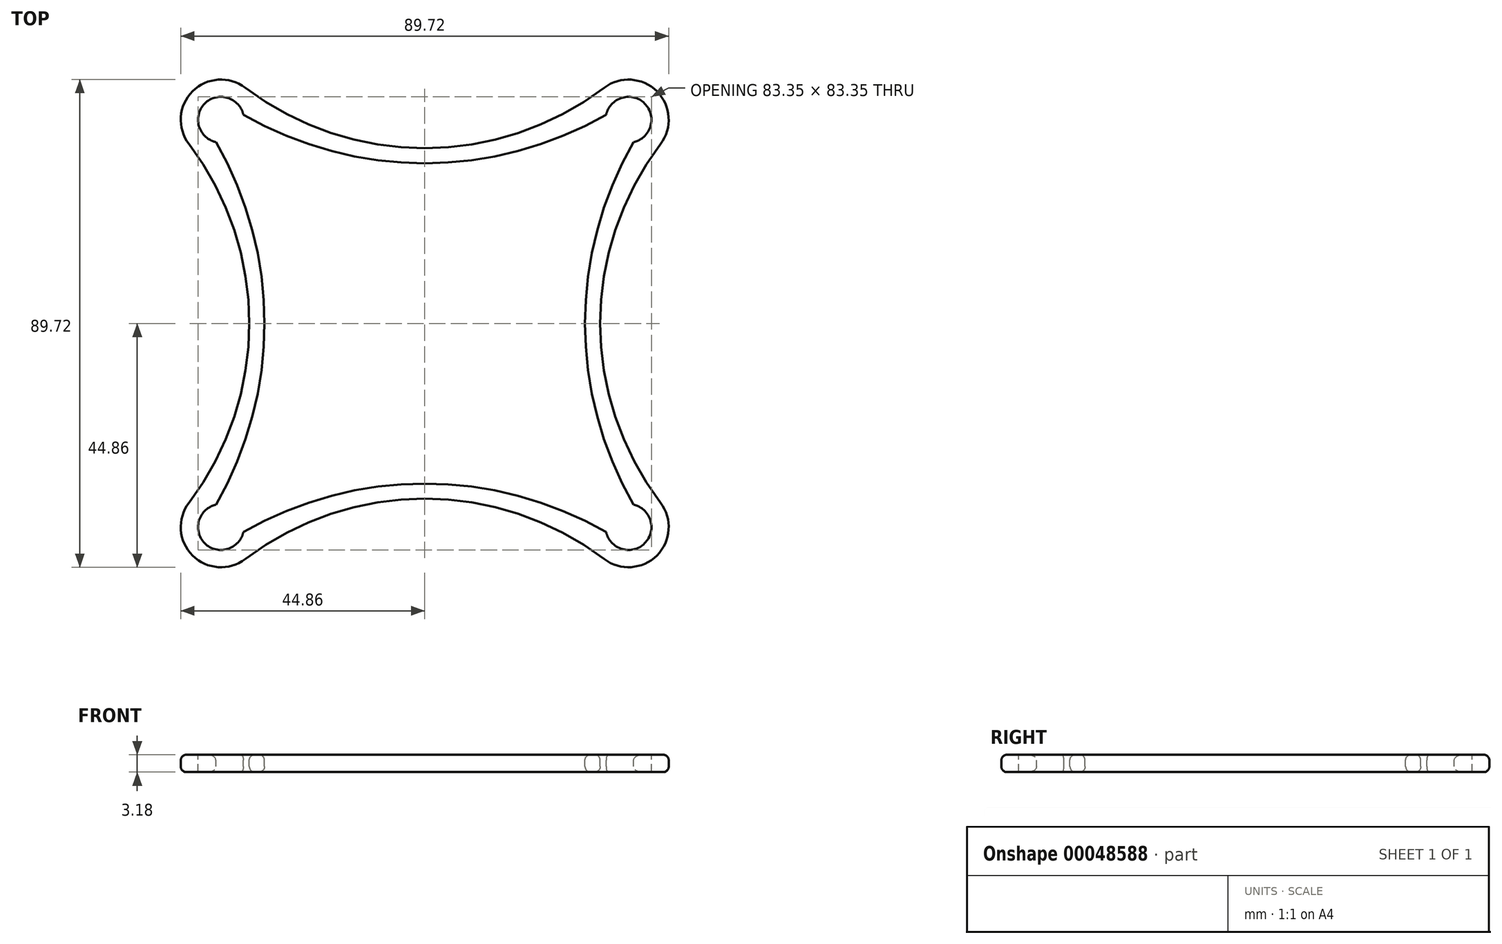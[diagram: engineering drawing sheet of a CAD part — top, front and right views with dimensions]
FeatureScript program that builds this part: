
annotation { "Feature Type Name" : "Feature", "Feature Type Description" : "" }
export const myFeature = defineFeature(function(context is Context, id is Id, definition is map)
    precondition{}
    {
        {
            var Q0;
            Q0=qCreatedBy(makeId("Top.planeOp"),FACE);
            var sketch = newSketch(context, id + "F0", { "sketchPlane" : qUnion([Q0])});
            skCircle(sketch, "E0", {"center": v(-37.47, 37.47) * mm, "radius": 4.22 * mm});
            skCircle(sketch, "E1", {"center": v(37.47, 37.47) * mm, "radius": 4.22 * mm});
            skCircle(sketch, "E2", {"center": v(37.47, -37.47) * mm, "radius": 4.22 * mm});
            skCircle(sketch, "E3", {"center": v(-37.47, -37.47) * mm, "radius": 4.22 * mm});
            skCircle(sketch, "E4", {"center": v(-37.47, 37.47) * mm, "radius": 7.4 * mm});
            skCircle(sketch, "E5", {"center": v(-37.47, -37.47) * mm, "radius": 7.4 * mm});
            skCircle(sketch, "E6", {"center": v(37.47, -37.47) * mm, "radius": 7.4 * mm});
            skCircle(sketch, "E7", {"center": v(37.47, 37.47) * mm, "radius": 7.4 * mm});
            skCircle(sketch, "E8", {"center": v(-96.14, 0) * mm, "radius": 66.68 * mm});
            skCircle(sketch, "E9", {"center": v(-86.87, 0) * mm, "radius": 54.61 * mm});
            skCircle(sketch, "E10", {"center": v(0, 96.14) * mm, "radius": 66.68 * mm});
            skCircle(sketch, "E11", {"center": v(0, 86.87) * mm, "radius": 54.61 * mm});
            skCircle(sketch, "E12", {"center": v(96.14, 0) * mm, "radius": 66.68 * mm});
            skCircle(sketch, "E13", {"center": v(86.87, 0) * mm, "radius": 54.61 * mm});
            skCircle(sketch, "E14", {"center": v(0, -96.14) * mm, "radius": 66.68 * mm});
            skCircle(sketch, "E15", {"center": v(0, -86.87) * mm, "radius": 54.61 * mm});
            skSolve(sketch);
        }
        {
            var Q0;
            {var subQ3=sQuery(id+"F0.wireOp",EDGE,"E4");var subQ5=sQuery(id+"F0.wireOp",EDGE,"E9");var subQ7=makeQuery(id+"F0.imprint","INTERSECT",VERTEX,{"derivedFrom":[subQ3,subQ5]});Q0=makeQuery(id+"F0.imprint","IMPRINT",FACE,{"disambiguationData":[TD([[makeQuery(id+"F0.imprint","IMPRINT",EDGE,{"disambiguationData":[TD([[subQ7,-1.0]])],"derivedFrom":subQ3}),-1.0]])]});}
            var Q1;
            {var subQ0=sQuery(id+"F0.wireOp",EDGE,"E8");var subQ1=sQuery(id+"F0.wireOp",EDGE,"E0");var subQ2=makeQuery(id+"F0.imprint","INTERSECT",VERTEX,{"disambiguationData":[OD(0.0)],"derivedFrom":[subQ1,subQ0]});Q1=makeQuery(id+"F0.imprint","IMPRINT",FACE,{"disambiguationData":[TD([[makeQuery(id+"F0.imprint","IMPRINT",EDGE,{"disambiguationData":[TD([[subQ2,-1.0]])],"derivedFrom":subQ1}),-1.0]])]});}
            var Q2;
            {var subQ0=sQuery(id+"F0.wireOp",EDGE,"E10");var subQ1=sQuery(id+"F0.wireOp",EDGE,"E0");var subQ2=makeQuery(id+"F0.imprint","INTERSECT",VERTEX,{"disambiguationData":[OD(0.0)],"derivedFrom":[subQ1,subQ0]});Q2=makeQuery(id+"F0.imprint","IMPRINT",FACE,{"disambiguationData":[TD([[makeQuery(id+"F0.imprint","IMPRINT",EDGE,{"disambiguationData":[TD([[subQ2,-1.0]])],"derivedFrom":subQ1}),-1.0]])]});}
            var Q3;
            {var subQ0=sQuery(id+"F0.wireOp",EDGE,"E0");var subQ1=sQuery(id+"F0.wireOp",EDGE,"E10");var subQ3=makeQuery(id+"F0.imprint","INTERSECT",VERTEX,{"disambiguationData":[OD(0.0)],"derivedFrom":[subQ0,subQ1]});Q3=makeQuery(id+"F0.imprint","IMPRINT",FACE,{"disambiguationData":[TD([[makeQuery(id+"F0.imprint","IMPRINT",EDGE,{"disambiguationData":[TD([[subQ3,1.0]])],"derivedFrom":subQ0}),-1.0]])]});}
            var Q4;
            {var subQ0=sQuery(id+"F0.wireOp",EDGE,"E11");var subQ3=sQuery(id+"F0.wireOp",EDGE,"E4");var subQ4=makeQuery(id+"F0.imprint","INTERSECT",VERTEX,{"derivedFrom":[subQ3,subQ0]});Q4=makeQuery(id+"F0.imprint","IMPRINT",FACE,{"disambiguationData":[TD([[makeQuery(id+"F0.imprint","IMPRINT",EDGE,{"disambiguationData":[TD([[subQ4,1.0]])],"derivedFrom":subQ3}),-1.0]])]});}
            var Q5;
            {var subQ0=sQuery(id+"F0.wireOp",EDGE,"E10");var subQ1=sQuery(id+"F0.wireOp",EDGE,"E1");var subQ5=makeQuery(id+"F0.imprint","INTERSECT",VERTEX,{"disambiguationData":[OD(0.0)],"derivedFrom":[subQ1,subQ0]});Q5=makeQuery(id+"F0.imprint","IMPRINT",FACE,{"disambiguationData":[TD([[makeQuery(id+"F0.imprint","IMPRINT",EDGE,{"disambiguationData":[TD([[subQ5,1.0]])],"derivedFrom":subQ1}),-1.0]])]});}
            var Q6;
            {var subQ1=sQuery(id+"F0.wireOp",EDGE,"E1");var subQ5=sQuery(id+"F0.wireOp",EDGE,"E10");var subQ6=makeQuery(id+"F0.imprint","INTERSECT",VERTEX,{"disambiguationData":[OD(1.0)],"derivedFrom":[subQ1,subQ5]});Q6=makeQuery(id+"F0.imprint","IMPRINT",FACE,{"disambiguationData":[TD([[makeQuery(id+"F0.imprint","IMPRINT",EDGE,{"disambiguationData":[TD([[subQ6,1.0]])],"derivedFrom":subQ1}),-1.0]])]});}
            var Q7;
            {var subQ0=sQuery(id+"F0.wireOp",EDGE,"E12");var subQ3=sQuery(id+"F0.wireOp",EDGE,"E1");var subQ4=makeQuery(id+"F0.imprint","INTERSECT",VERTEX,{"disambiguationData":[OD(0.0)],"derivedFrom":[subQ3,subQ0]});Q7=makeQuery(id+"F0.imprint","IMPRINT",FACE,{"disambiguationData":[TD([[makeQuery(id+"F0.imprint","IMPRINT",EDGE,{"disambiguationData":[TD([[subQ4,-1.0]])],"derivedFrom":subQ3}),-1.0]])]});}
            var Q8;
            {var subQ0=sQuery(id+"F0.wireOp",EDGE,"E12");var subQ3=sQuery(id+"F0.wireOp",EDGE,"E6");var subQ4=makeQuery(id+"F0.imprint","INTERSECT",VERTEX,{"disambiguationData":[OD(1.0)],"derivedFrom":[subQ3,subQ0]});Q8=makeQuery(id+"F0.imprint","IMPRINT",FACE,{"disambiguationData":[TD([[makeQuery(id+"F0.imprint","IMPRINT",EDGE,{"disambiguationData":[TD([[subQ4,1.0]])],"derivedFrom":subQ3}),-1.0]])]});}
            var Q9;
            {var subQ0=sQuery(id+"F0.wireOp",EDGE,"E12");var subQ1=sQuery(id+"F0.wireOp",EDGE,"E2");var subQ5=makeQuery(id+"F0.imprint","INTERSECT",VERTEX,{"disambiguationData":[OD(0.0)],"derivedFrom":[subQ1,subQ0]});Q9=makeQuery(id+"F0.imprint","IMPRINT",FACE,{"disambiguationData":[TD([[makeQuery(id+"F0.imprint","IMPRINT",EDGE,{"disambiguationData":[TD([[subQ5,1.0]])],"derivedFrom":subQ1}),-1.0]])]});}
            var Q10;
            {var subQ0=sQuery(id+"F0.wireOp",EDGE,"E12");var subQ1=sQuery(id+"F0.wireOp",EDGE,"E2");var subQ2=makeQuery(id+"F0.imprint","INTERSECT",VERTEX,{"disambiguationData":[OD(1.0)],"derivedFrom":[subQ1,subQ0]});Q10=makeQuery(id+"F0.imprint","IMPRINT",FACE,{"disambiguationData":[TD([[makeQuery(id+"F0.imprint","IMPRINT",EDGE,{"disambiguationData":[TD([[subQ2,1.0]])],"derivedFrom":subQ1}),-1.0]])]});}
            var Q11;
            {var subQ0=sQuery(id+"F0.wireOp",EDGE,"E14");var subQ3=sQuery(id+"F0.wireOp",EDGE,"E2");var subQ4=makeQuery(id+"F0.imprint","INTERSECT",VERTEX,{"disambiguationData":[OD(0.0)],"derivedFrom":[subQ3,subQ0]});Q11=makeQuery(id+"F0.imprint","IMPRINT",FACE,{"disambiguationData":[TD([[makeQuery(id+"F0.imprint","IMPRINT",EDGE,{"disambiguationData":[TD([[subQ4,-1.0]])],"derivedFrom":subQ3}),-1.0]])]});}
            var Q12;
            {var subQ3=sQuery(id+"F0.wireOp",EDGE,"E5");var subQ5=sQuery(id+"F0.wireOp",EDGE,"E14");var subQ7=makeQuery(id+"F0.imprint","INTERSECT",VERTEX,{"disambiguationData":[OD(1.0)],"derivedFrom":[subQ3,subQ5]});Q12=makeQuery(id+"F0.imprint","IMPRINT",FACE,{"disambiguationData":[TD([[makeQuery(id+"F0.imprint","IMPRINT",EDGE,{"disambiguationData":[TD([[subQ7,1.0]])],"derivedFrom":subQ3}),-1.0]])]});}
            var Q13;
            {var subQ0=sQuery(id+"F0.wireOp",EDGE,"E3");var subQ1=sQuery(id+"F0.wireOp",EDGE,"E14");var subQ3=makeQuery(id+"F0.imprint","INTERSECT",VERTEX,{"disambiguationData":[OD(0.0)],"derivedFrom":[subQ0,subQ1]});Q13=makeQuery(id+"F0.imprint","IMPRINT",FACE,{"disambiguationData":[TD([[makeQuery(id+"F0.imprint","IMPRINT",EDGE,{"disambiguationData":[TD([[subQ3,-1.0]])],"derivedFrom":subQ0}),-1.0]])]});}
            var Q14;
            {var subQ1=sQuery(id+"F0.wireOp",EDGE,"E3");var subQ5=sQuery(id+"F0.wireOp",EDGE,"E8");var subQ7=makeQuery(id+"F0.imprint","INTERSECT",VERTEX,{"disambiguationData":[OD(0.0)],"derivedFrom":[subQ1,subQ5]});Q14=makeQuery(id+"F0.imprint","IMPRINT",FACE,{"disambiguationData":[TD([[makeQuery(id+"F0.imprint","IMPRINT",EDGE,{"disambiguationData":[TD([[subQ7,-1.0]])],"derivedFrom":subQ1}),-1.0]])]});}
            var Q15;
            {var subQ0=sQuery(id+"F0.wireOp",EDGE,"E8");var subQ3=sQuery(id+"F0.wireOp",EDGE,"E3");var subQ5=makeQuery(id+"F0.imprint","INTERSECT",VERTEX,{"disambiguationData":[OD(0.0)],"derivedFrom":[subQ3,subQ0]});Q15=makeQuery(id+"F0.imprint","IMPRINT",FACE,{"disambiguationData":[TD([[makeQuery(id+"F0.imprint","IMPRINT",EDGE,{"disambiguationData":[TD([[subQ5,1.0]])],"derivedFrom":subQ3}),-1.0]])]});}
            var Q16;
            {var subQ0=sQuery(id+"F0.wireOp",EDGE,"E12");var subQ3=sQuery(id+"F0.wireOp",EDGE,"E1");var subQ6=makeQuery(id+"F0.imprint","INTERSECT",VERTEX,{"disambiguationData":[OD(0.0)],"derivedFrom":[subQ3,subQ0]});Q16=makeQuery(id+"F0.imprint","IMPRINT",FACE,{"disambiguationData":[TD([[makeQuery(id+"F0.imprint","IMPRINT",EDGE,{"disambiguationData":[TD([[subQ6,1.0]])],"derivedFrom":subQ3}),-1.0]])]});}
            extrude(context, id + "F1", {"entities" : qUnion([Q0, Q1, Q2, Q3, Q4, Q5, Q6, Q7, Q8, Q9, Q10, Q11, Q12, Q13, Q14, Q15, Q16]), "oppositeDirection" : true, "depth" : 3.17 * mm});
        }
        {
            var Q0;
            Q0=makeQuery(id+"F1.opExtrude","CAP_EDGE",EDGE,{"disambiguationData":[OSD([sQuery(id+"F0.wireOp",EDGE,"a5322268-e1dc-436a-8e73-038b822e4c18")])],"isStart":false});
            var Q1;
            Q1=makeQuery(id+"F1.opExtrude","CAP_EDGE",EDGE,{"disambiguationData":[OSD([sQuery(id+"F0.wireOp",EDGE,"E7")])],"isStart":false});
            var Q2;
            Q2=makeQuery(id+"F1.opExtrude","CAP_EDGE",EDGE,{"disambiguationData":[OSD([sQuery(id+"F0.wireOp",EDGE,"1cb2681a-f61c-4038-b64f-4d8f3c1fa337")])],"isStart":true});
            var Q3;
            Q3=makeQuery(id+"F1.opExtrude","CAP_EDGE",EDGE,{"disambiguationData":[OSD([sQuery(id+"F0.wireOp",EDGE,"1cb2681a-f61c-4038-b64f-4d8f3c1fa337")])],"isStart":false});
            var Q4;
            Q4=makeQuery(id+"F1.opExtrude","CAP_EDGE",EDGE,{"disambiguationData":[OSD([sQuery(id+"F0.wireOp",EDGE,"E6")])],"isStart":false});
            var Q5;
            Q5=makeQuery(id+"F1.opExtrude","CAP_EDGE",EDGE,{"disambiguationData":[OSD([sQuery(id+"F0.wireOp",EDGE,"90b38568-d89f-4760-90db-baeff50cd179")])],"isStart":false});
            var Q6;
            Q6=makeQuery(id+"F1.opExtrude","CAP_EDGE",EDGE,{"disambiguationData":[OSD([sQuery(id+"F0.wireOp",EDGE,"E5")])],"isStart":false});
            var Q7;
            Q7=makeQuery(id+"F1.opExtrude","CAP_EDGE",EDGE,{"disambiguationData":[OSD([sQuery(id+"F0.wireOp",EDGE,"a8b6ce6c-9c41-4146-a937-b0af54ecc49b")])],"isStart":false});
            var Q8;
            Q8=makeQuery(id+"F1.opExtrude","CAP_EDGE",EDGE,{"disambiguationData":[OSD([sQuery(id+"F0.wireOp",EDGE,"E4")])],"isStart":false});
            var Q9;
            Q9=makeQuery(id+"F1.opExtrude","CAP_EDGE",EDGE,{"disambiguationData":[OSD([sQuery(id+"F0.wireOp",EDGE,"E6")])],"isStart":true});
            var Q10;
            Q10=makeQuery(id+"F1.opExtrude","CAP_EDGE",EDGE,{"disambiguationData":[OSD([sQuery(id+"F0.wireOp",EDGE,"90b38568-d89f-4760-90db-baeff50cd179")])],"isStart":true});
            var Q11;
            Q11=makeQuery(id+"F1.opExtrude","CAP_EDGE",EDGE,{"disambiguationData":[OSD([sQuery(id+"F0.wireOp",EDGE,"E5")])],"isStart":true});
            var Q12;
            Q12=makeQuery(id+"F1.opExtrude","CAP_EDGE",EDGE,{"disambiguationData":[OSD([sQuery(id+"F0.wireOp",EDGE,"a8b6ce6c-9c41-4146-a937-b0af54ecc49b")])],"isStart":true});
            var Q13;
            Q13=makeQuery(id+"F1.opExtrude","CAP_EDGE",EDGE,{"disambiguationData":[OSD([sQuery(id+"F0.wireOp",EDGE,"a5322268-e1dc-436a-8e73-038b822e4c18")])],"isStart":true});
            var Q14;
            Q14=makeQuery(id+"F1.opExtrude","CAP_EDGE",EDGE,{"disambiguationData":[OSD([sQuery(id+"F0.wireOp",EDGE,"E7")])],"isStart":true});
            var Q15;
            Q15=makeQuery(id+"F1.opExtrude","CAP_EDGE",EDGE,{"disambiguationData":[OSD([sQuery(id+"F0.wireOp",EDGE,"E4")])],"isStart":true});
            fillet(context, id + "F2", {"entities" : qUnion([Q0, Q1, Q2, Q3, Q4, Q5, Q6, Q7, Q8, Q9, Q10, Q11, Q12, Q13, Q14, Q15]), "radius" : 1.02 * mm, "tangentPropagation" : true, "allowEdgeOverflow" : false});
        }
        {
            var Q0;
            Q0=makeQuery(id+"F1.opExtrude","CAP_EDGE",EDGE,{"disambiguationData":[OSD([sQuery(id+"F0.wireOp",EDGE,"E14")])],"isStart":true});
            var Q1;
            Q1=makeQuery(id+"F1.opExtrude","CAP_EDGE",EDGE,{"disambiguationData":[OSD([sQuery(id+"F0.wireOp",EDGE,"E8")])],"isStart":true});
            var Q2;
            Q2=makeQuery(id+"F1.opExtrude","CAP_EDGE",EDGE,{"disambiguationData":[OSD([sQuery(id+"F0.wireOp",EDGE,"E12")])],"isStart":true});
            var Q3;
            Q3=makeQuery(id+"F1.opExtrude","CAP_EDGE",EDGE,{"disambiguationData":[OSD([sQuery(id+"F0.wireOp",EDGE,"E10")])],"isStart":true});
            var Q4;
            Q4=makeQuery(id+"F1.opExtrude","CAP_EDGE",EDGE,{"disambiguationData":[OSD([sQuery(id+"F0.wireOp",EDGE,"E12")])],"isStart":false});
            var Q5;
            Q5=makeQuery(id+"F1.opExtrude","CAP_EDGE",EDGE,{"disambiguationData":[OSD([sQuery(id+"F0.wireOp",EDGE,"E10")])],"isStart":false});
            var Q6;
            Q6=makeQuery(id+"F1.opExtrude","CAP_EDGE",EDGE,{"disambiguationData":[OSD([sQuery(id+"F0.wireOp",EDGE,"E8")])],"isStart":false});
            var Q7;
            Q7=makeQuery(id+"F1.opExtrude","CAP_EDGE",EDGE,{"disambiguationData":[OSD([sQuery(id+"F0.wireOp",EDGE,"E14")])],"isStart":false});
            fillet(context, id + "F3", {"entities" : qUnion([Q0, Q1, Q2, Q3, Q4, Q5, Q6, Q7]), "radius" : 1.02 * mm, "tangentPropagation" : true, "allowEdgeOverflow" : false});
        }
    });
